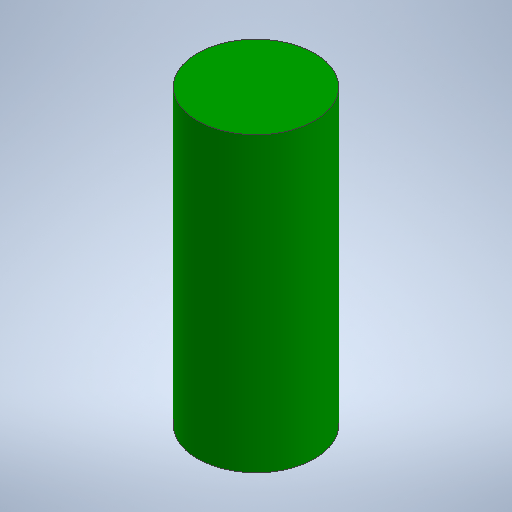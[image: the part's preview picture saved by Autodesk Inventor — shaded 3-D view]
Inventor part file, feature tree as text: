
AUTODESK INVENTOR PART (.ipt)
format: ipt  version: 2025.2 (Build 292293000, 293)  size: 223,744 bytes
history: native  units: mm
features: extrude x1, sketch x1
ambient origin geometry x8: Origin, YZ Plane, XZ Plane, XY Plane, X Axis, Y Axis, Z Axis, Center Point
bodies: Solid1 (feature_tree)
feature tree (2):
  extrude  "Extrusion1"  Depth=65.0mm TaperAngle=0.0deg
  sketch  "Sketch1"  dims[d0=26.0mm d1=65.0mm d2=0.0mm]
